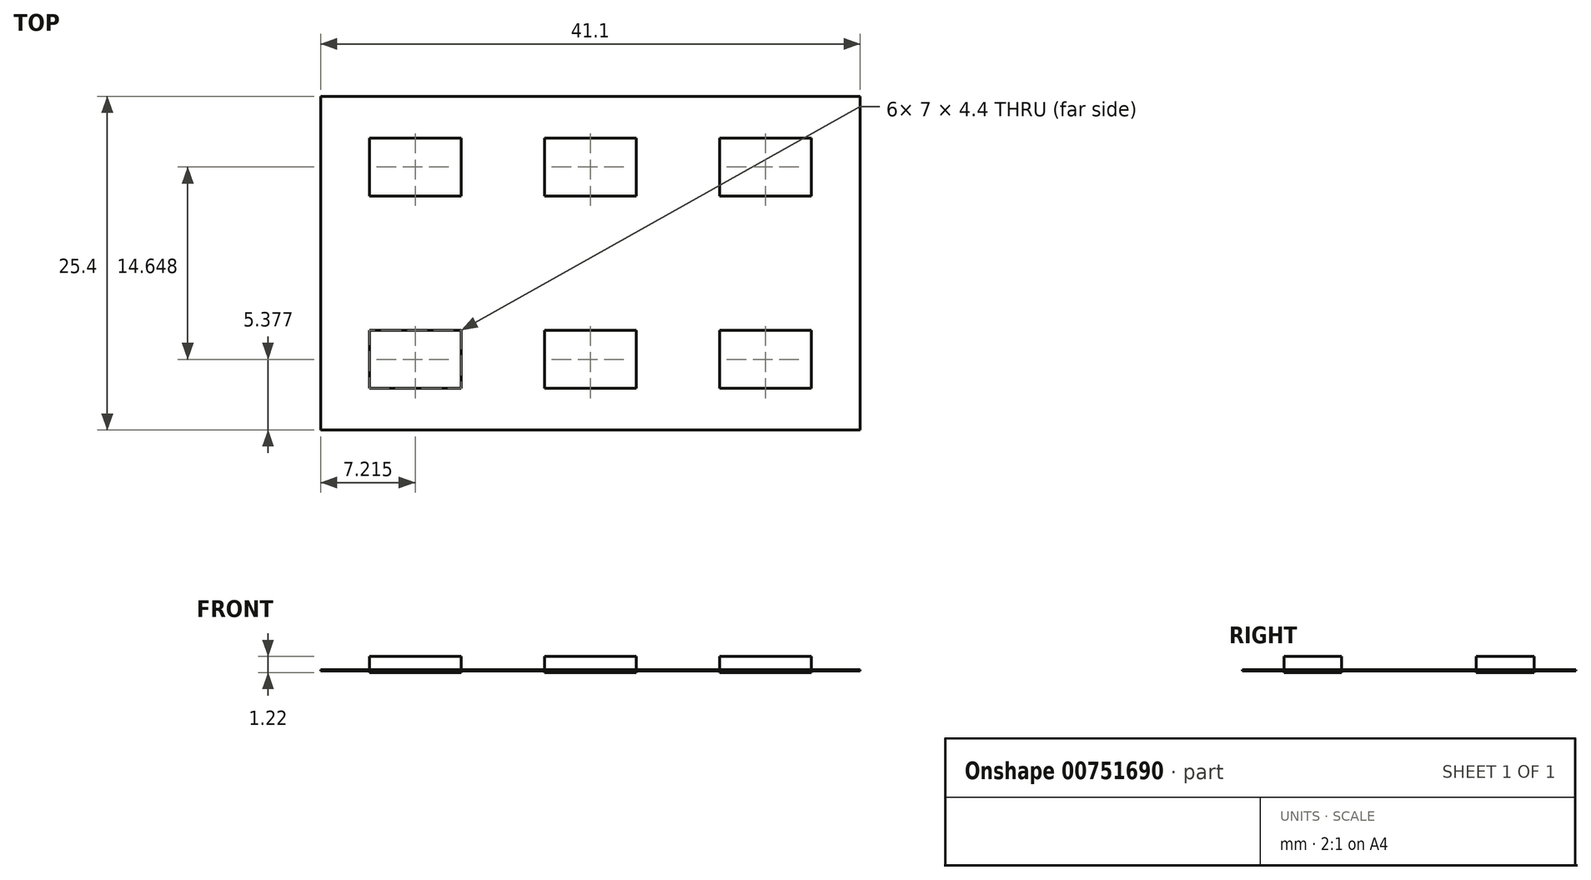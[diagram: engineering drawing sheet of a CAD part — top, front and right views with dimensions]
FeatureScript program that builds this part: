
annotation { "Feature Type Name" : "Feature", "Feature Type Description" : "" }
export const myFeature = defineFeature(function(context is Context, id is Id, definition is map)
    precondition{}
    {
        {
            var Q0;
            Q0=qCreatedBy(makeId("Top.planeOp"),FACE);
            var sketch = newSketch(context, id + "F0", { "sketchPlane" : qUnion([Q0])});
            skLineSegment(sketch, "E0.bottom", {"start": v(20.55, 12.7) * mm, "end": v(-20.55, 12.7) * mm});
            skLineSegment(sketch, "E0.top", {"start": v(20.55, -12.7) * mm, "end": v(-20.55, -12.7) * mm});
            skLineSegment(sketch, "E0.left", {"start": v(20.55, 12.7) * mm, "end": v(20.55, -12.7) * mm});
            skLineSegment(sketch, "E0.right", {"start": v(-20.55, 12.7) * mm, "end": v(-20.55, -12.7) * mm});
            skPoint(sketch, "E0.middle", {"position": v(0, 0) * mm});
            skSolve(sketch);
        }
        {
            var Q0;
            Q0 = qSketchRegion(id + "F0", true);
            extrude(context, id + "F1", {"entities" : qUnion([Q0]), "depth" : 0.08 * mm, "offsetDistance" : 25.4 * mm});
        }
        {
            var Q0;
            Q0=makeQuery(id+"F1.opExtrude","CAP_FACE",FACE,{"disambiguationData":[OSD([sQuery(id+"F0.wireOp",EDGE,"E0.bottom"),sQuery(id+"F0.wireOp",EDGE,"E0.top"),sQuery(id+"F0.wireOp",EDGE,"E0.left"),sQuery(id+"F0.wireOp",EDGE,"E0.right")])],"isStart":false});
            var sketch = newSketch(context, id + "F2", { "sketchPlane" : qUnion([Q0])});
            skLineSegment(sketch, "E1.bottom", {"start": v(-9.84, 5.13) * mm, "end": v(-16.84, 5.13) * mm});
            skLineSegment(sketch, "E1.top", {"start": v(-9.84, 9.53) * mm, "end": v(-16.84, 9.53) * mm});
            skLineSegment(sketch, "E1.left", {"start": v(-9.84, 5.13) * mm, "end": v(-9.84, 9.53) * mm});
            skLineSegment(sketch, "E1.right", {"start": v(-16.84, 5.13) * mm, "end": v(-16.84, 9.53) * mm});
            skPoint(sketch, "E1.middle", {"position": v(-13.34, 7.33) * mm});
            skLineSegment(sketch, "E2.0.1.0", {"start": v(-9.84, -9.52) * mm, "end": v(-16.84, -9.52) * mm});
            skLineSegment(sketch, "E2.0.1.1", {"start": v(-16.84, -9.52) * mm, "end": v(-16.84, -5.12) * mm});
            skLineSegment(sketch, "E2.0.1.2", {"start": v(-9.84, -5.12) * mm, "end": v(-16.84, -5.12) * mm});
            skLineSegment(sketch, "E2.0.1.3", {"start": v(-9.84, -9.52) * mm, "end": v(-9.84, -5.12) * mm});
            skLineSegment(sketch, "E2.1.0.0", {"start": v(3.5, 5.13) * mm, "end": v(-3.5, 5.13) * mm});
            skLineSegment(sketch, "E2.1.0.1", {"start": v(-3.5, 5.13) * mm, "end": v(-3.5, 9.53) * mm});
            skLineSegment(sketch, "E2.1.0.2", {"start": v(3.5, 9.53) * mm, "end": v(-3.5, 9.53) * mm});
            skLineSegment(sketch, "E2.1.0.3", {"start": v(3.5, 5.13) * mm, "end": v(3.5, 9.53) * mm});
            skLineSegment(sketch, "E2.1.1.0", {"start": v(3.5, -9.52) * mm, "end": v(-3.5, -9.52) * mm});
            skLineSegment(sketch, "E2.1.1.1", {"start": v(-3.5, -9.52) * mm, "end": v(-3.5, -5.12) * mm});
            skLineSegment(sketch, "E2.1.1.2", {"start": v(3.5, -5.12) * mm, "end": v(-3.5, -5.12) * mm});
            skLineSegment(sketch, "E2.1.1.3", {"start": v(3.5, -9.52) * mm, "end": v(3.5, -5.12) * mm});
            skLineSegment(sketch, "E2.2.0.0", {"start": v(16.83, 5.13) * mm, "end": v(9.83, 5.13) * mm});
            skLineSegment(sketch, "E2.2.0.1", {"start": v(9.83, 5.13) * mm, "end": v(9.83, 9.53) * mm});
            skLineSegment(sketch, "E2.2.0.2", {"start": v(16.83, 9.53) * mm, "end": v(9.83, 9.53) * mm});
            skLineSegment(sketch, "E2.2.0.3", {"start": v(16.83, 5.13) * mm, "end": v(16.83, 9.53) * mm});
            skLineSegment(sketch, "E2.2.1.0", {"start": v(16.83, -9.52) * mm, "end": v(9.83, -9.52) * mm});
            skLineSegment(sketch, "E2.2.1.1", {"start": v(9.83, -9.52) * mm, "end": v(9.83, -5.12) * mm});
            skLineSegment(sketch, "E2.2.1.2", {"start": v(16.83, -5.12) * mm, "end": v(9.83, -5.12) * mm});
            skLineSegment(sketch, "E2.2.1.3", {"start": v(16.83, -9.52) * mm, "end": v(16.83, -5.12) * mm});
            skLineSegment(sketch, "E2.direction1", {"start": v(-16.84, 5.13) * mm, "end": v(-3.5, 5.13) * mm, "construction": true});
            skLineSegment(sketch, "E2.direction2", {"start": v(-16.84, 5.13) * mm, "end": v(-16.84, -9.52) * mm, "construction": true});
            skSolve(sketch);
        }
        {
            var Q0;
            Q0 = qSketchRegion(id + "F2", true);
            extrude(context, id + "F3", {"entities" : qUnion([Q0]), "operationType" : NewBodyOperationType.ADD, "depth" : 1.02 * mm, "offsetDistance" : 25.4 * mm});
        }
        {
            var Q0;
            Q0 = qSketchRegion(id + "F2", true);
            extrude(context, id + "F4", {"entities" : qUnion([Q0]), "operationType" : NewBodyOperationType.ADD, "oppositeDirection" : true, "depth" : 0.2 * mm, "offsetDistance" : 25.4 * mm});
        }
    });
